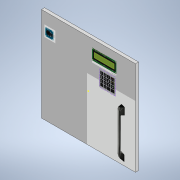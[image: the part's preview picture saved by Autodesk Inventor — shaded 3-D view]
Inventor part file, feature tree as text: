
AUTODESK INVENTOR PART (.ipt)
format: ipt  version: 2022 (Build 260153000, 153)  size: 1,077,248 bytes
history: native  units: mm
features: other x14, sketch x13, extrude x1
ambient origin geometry x8: Origin, YZ Plane, XZ Plane, XY Plane, X Axis, Y Axis, Z Axis, Center Point
bodies: Solid1 (feature_tree)
feature tree (28):
  extrude  "Extrusion1"  Depth=304.8mm
  sketch  "Sketch2"  dims[d2=10.0mm d3=0.0mm]
  sketch  "Sketch3"
  sketch  "Sketch4"
  sketch  "Sketch5"
  sketch  "Sketch6"
  sketch  "Sketch7"
  sketch  "Sketch8"
  other  "Decal1"
  other  "Decal2"
  other  "Decal3"
  other  "Decal4"
  other  "Decal5"
  other  "Decal6"
  sketch  "Sketch10"
  sketch  "Sketch11"
  sketch  "Sketch12"
  other  "Decal7"
  other  "Decal8"
  sketch  "Sketch1"  dims[d0=304.8mm d1=304.8mm]
  other  "Image1"
  other  "Image3"
  other  "Image4"
  other  "Image6"
  sketch  "Sketch9"
  other  "Image8"
  sketch  "Sketch13"
  other  "Image9"
